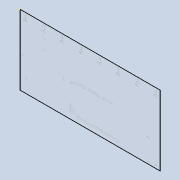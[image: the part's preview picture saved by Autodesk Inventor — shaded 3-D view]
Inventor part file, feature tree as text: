
AUTODESK INVENTOR PART (.ipt)
format: ipt  version: 2022 (Build 260153000, 153)  size: 696,832 bytes
history: native  units: in
note: dims shown in document units (in); Inventor stores cm internally (conversion verified against a paired STEP export)
features: sketch x1, extrude x1, other x1
ambient origin geometry x8: Origin, YZ Plane, XZ Plane, XY Plane, X Axis, Y Axis, Z Axis, Center Point
bodies: Solid1 (feature_tree)
feature tree (3):
  sketch  "Sketch1"  dims[d5=0.01in d6=0.0in d8=9.0in]
  extrude  "Extrusion1"  Depth=9.0in
  other  "Image2"
